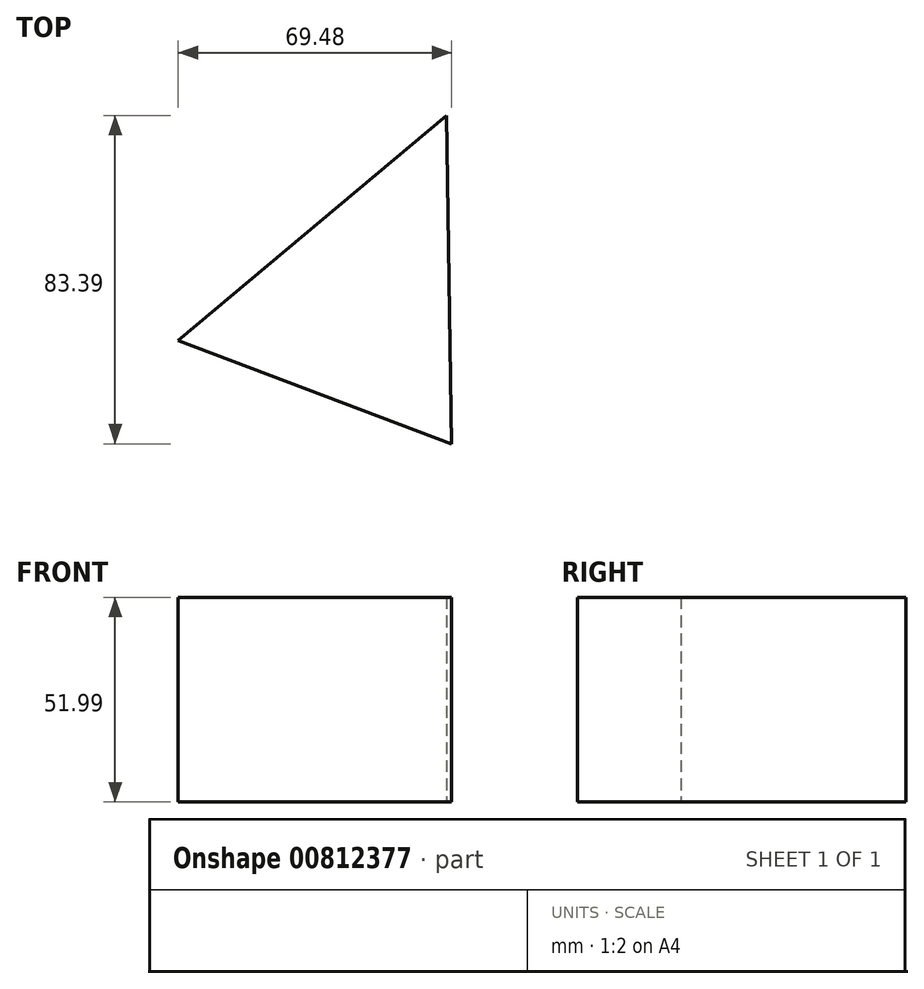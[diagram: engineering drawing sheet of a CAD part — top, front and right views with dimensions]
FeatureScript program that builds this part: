
annotation { "Feature Type Name" : "Feature", "Feature Type Description" : "" }
export const myFeature = defineFeature(function(context is Context, id is Id, definition is map)
    precondition{}
    {
        {
            var Q0;
            Q0=qCreatedBy(makeId("Top.planeOp"),FACE);
            var sketch = newSketch(context, id + "F0", { "sketchPlane" : qUnion([Q0])});
            skLineSegment(sketch, "E0", {"start": v(68.16, 57.18) * mm, "end": v(0, 0) * mm});
            skLineSegment(sketch, "E1", {"start": v(0, 0) * mm, "end": v(69.48, -26.21) * mm});
            skLineSegment(sketch, "E2", {"start": v(69.48, -26.21) * mm, "end": v(68.16, 57.18) * mm});
            skSolve(sketch);
        }
        {
            var Q0;
            Q0 = qSketchRegion(id + "F0", true);
            extrude(context, id + "F1", {"entities" : qUnion([Q0]), "depth" : 52 * mm, "offsetDistance" : 25.4 * mm});
        }
    });
